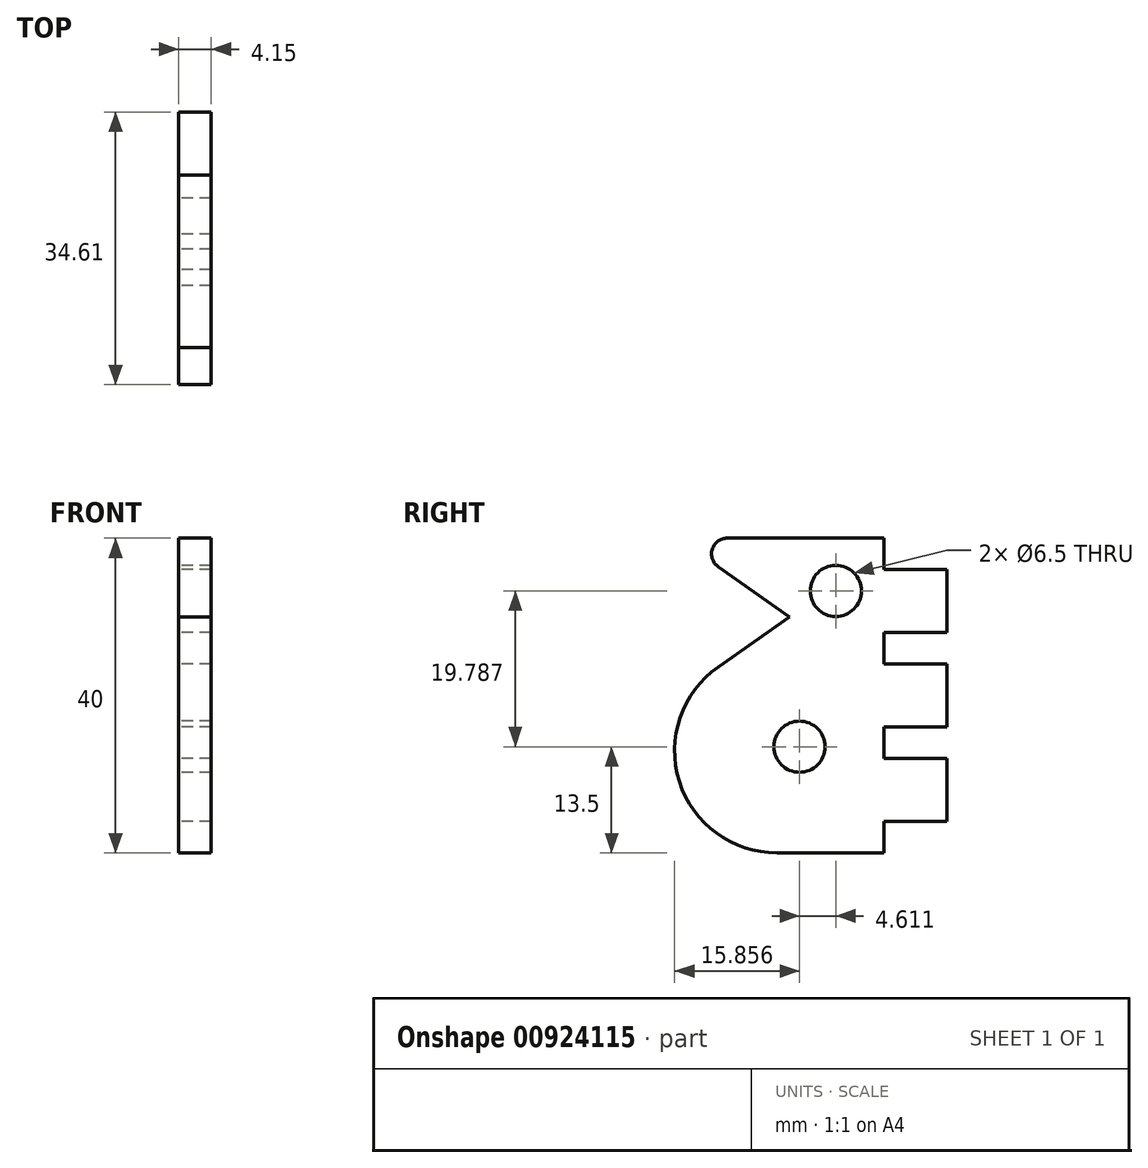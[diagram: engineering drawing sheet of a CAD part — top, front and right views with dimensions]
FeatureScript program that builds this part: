
annotation { "Feature Type Name" : "Feature", "Feature Type Description" : "" }
export const myFeature = defineFeature(function(context is Context, id is Id, definition is map)
    precondition{}
    {
        {
            var Q0;
            Q0=qCreatedBy(makeId("Right.planeOp"),FACE);
            var sketch = newSketch(context, id + "F0", { "sketchPlane" : qUnion([Q0])});
            skLineSegment(sketch, "E0", {"start": v(0, 0) * mm, "end": v(0, 4) * mm});
            skLineSegment(sketch, "E1", {"start": v(0, 28) * mm, "end": v(8, 28) * mm});
            skLineSegment(sketch, "E2", {"start": v(8, 28) * mm, "end": v(8, 36) * mm});
            skLineSegment(sketch, "E3", {"start": v(-21.07, 36.35) * mm, "end": v(-12, 30) * mm});
            skLineSegment(sketch, "E4", {"start": v(-12, 30) * mm, "end": v(-21.07, 23.65) * mm});
            skLineSegment(sketch, "E5", {"start": v(-13.61, 0) * mm, "end": v(0, 0) * mm});
            skLineSegment(sketch, "E6", {"start": v(-12, 30) * mm, "end": v(0, 30) * mm, "construction": true});
            skArc(sketch, "E7", {"start": v(-21.07, 23.65) * mm, "mid": v(-26.01, 9.1) * mm, "end": v(-13.61, 0) * mm});
            skLineSegment(sketch, "E8", {"start": v(0, 40) * mm, "end": v(-19.92, 40) * mm});
            skArc(sketch, "E9", {"start": v(-19.92, 40) * mm, "mid": v(-21.83, 38.6) * mm, "end": v(-21.07, 36.35) * mm});
            skLineSegment(sketch, "E10", {"start": v(0, 40) * mm, "end": v(0, 36) * mm});
            skLineSegment(sketch, "E11", {"start": v(0, 36) * mm, "end": v(8, 36) * mm});
            skCircle(sketch, "E12", {"center": v(-10.75, 13.5) * mm, "radius": 3.25 * mm});
            skLineSegment(sketch, "E13", {"start": v(0, 4) * mm, "end": v(8, 4) * mm});
            skLineSegment(sketch, "E14", {"start": v(8, 4) * mm, "end": v(8, 12) * mm});
            skLineSegment(sketch, "E15", {"start": v(8, 12) * mm, "end": v(0, 12) * mm});
            skLineSegment(sketch, "E16", {"start": v(0, 12) * mm, "end": v(0, 16) * mm});
            skLineSegment(sketch, "E17", {"start": v(0, 16) * mm, "end": v(8, 16) * mm});
            skLineSegment(sketch, "E18", {"start": v(8, 16) * mm, "end": v(8, 24) * mm});
            skLineSegment(sketch, "E19", {"start": v(8, 24) * mm, "end": v(0, 24) * mm});
            skLineSegment(sketch, "E20", {"start": v(0, 24) * mm, "end": v(0, 28) * mm});
            skCircle(sketch, "E21", {"center": v(-6.14, 33.29) * mm, "radius": 3.25 * mm});
            skCircle(sketch, "E22", {"center": v(-6.14, 33.29) * mm, "radius": 6.72 * mm, "construction": true});
            skPoint(sketch, "E22.third.point", {"position": v(-5.94, 40) * mm});
            skSolve(sketch);
        }
        {
            var Q0;
            Q0 = qSketchRegion(id + "F0", true);
            extrude(context, id + "F1", {"entities" : qUnion([Q0]), "depth" : 4.15 * mm, "offsetDistance" : 25 * mm});
        }
    });
